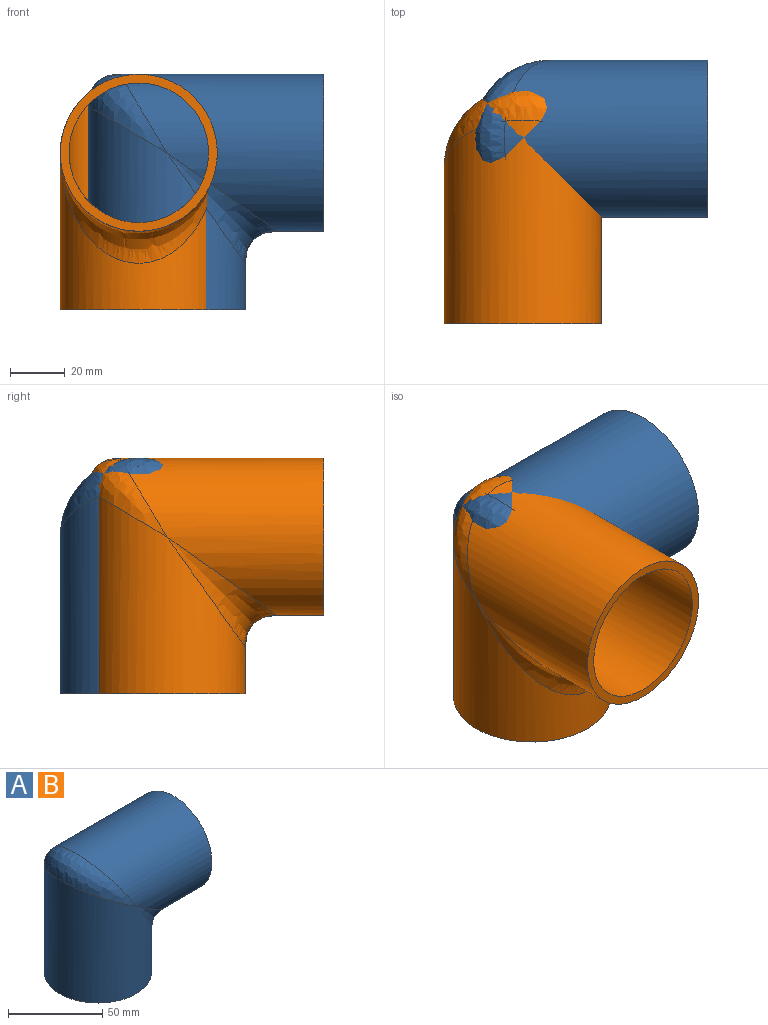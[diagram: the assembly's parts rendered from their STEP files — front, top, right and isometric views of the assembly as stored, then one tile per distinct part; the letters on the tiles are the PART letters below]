
ASSEMBLY  parts=2 mates=1
PART A: 8 faces, bbox 85.7x57.2x85.7 mm
  f0: cylinder r=28.57mm len=74.08mm, axis (1,0,0), area 8929.3mm2, adj f2,f6,f7
  f1: cylinder r=28.57mm len=74.08mm, axis (0,0,1), area 8929.3mm2, adj f3,f6,f7
  f2: plane 57.15x57.15mm, normal (1,0,0), area 538.4mm2, adj f0,f4
  f3: plane 57.15x57.15mm, normal (0,0,-1), area 538.4mm2, adj f1,f5
  f4: cylinder r=25.4mm len=82.55mm, axis (1,0,0), area 9120.7mm2, adj f2,f5
  f5: cylinder r=25.4mm len=82.55mm, axis (0,0,1), area 9120.7mm2, adj f3,f4
  f6: bspline ~57.15x40.23mm, area 703.6mm2, adj f0,f1
  f7: bspline ~57.15x28.58mm, area 0mm2, adj f0,f1
PART B: same geometry as A
PLACE A t=(-201.37,-25.76,-7.71)mm
PLACE B rot(axis=(0,0,-1),90deg) t=(-211.53,-35.92,-7.71)mm
MATE fastened B.f1 <-> A.f3  axis (0,0,-1) through (-211.53,-35.92,-7.71)mm
